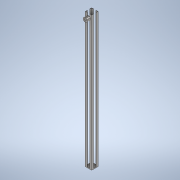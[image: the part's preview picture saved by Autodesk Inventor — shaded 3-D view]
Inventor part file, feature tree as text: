
AUTODESK INVENTOR PART (.ipt)
format: ipt  version: 2020 (Build 240168000, 168)  size: 164,864 bytes
history: native  units: mm
features: extrude x6, sketch x6
ambient origin geometry x8: Origin, YZ Plane, XZ Plane, XY Plane, X Axis, Y Axis, Z Axis, Center Point
bodies: Solid1 (feature_tree)
feature tree (12):
  extrude  "Extrusion1"  Depth=38.0mm
  extrude  "Extrusion5"  Depth=800.0mm TaperAngle=0.0deg
  sketch  "Sketch6"  dims[d20=15.0mm d21=55.0mm]
  extrude  "Extrusion6"  Depth=15.0mm
  extrude  "Extrusion7"  Depth=15.0mm
  extrude  "Extrusion8"  Depth=35.0mm
  extrude  "Extrusion9"  Depth=800.0mm TaperAngle=0.0deg
  sketch  "Sketch1"  dims[d0=38.0mm d1=38.0mm]
  sketch  "Sketch5"  dims[d2=5.0mm d3=0.0mm d18=800.0mm d19=0.0mm]
  sketch  "Sketch7"  dims[d22=55.0mm d23=15.0mm]
  sketch  "Sketch8"  dims[d24=35.0mm d25=35.0mm]
  sketch  "Sketch9"  dims[d26=800.0mm d27=0.0mm d28=800.0mm d29=0.0mm d30=10.0mm d31=2.0mm d32=0.0mm d33=13.0mm d34=20.0mm d35=0.0mm]
